# Revit family: ACV-5-Series
name_source: partatom
category: Generic Models
revit_build: Autodesk Revit 2014 (Build: 20130308_1515(x64)
units: mm (PartAtom-declared; Revit-internal decimal feet)

## types (5) — shared parameters
Description = BEECO ACV Angle Series
Manufacturer = MIFAB
Mateiral = Iron, Cast
URL = www.mifab.com

## per-type parameters (varying)
- ACV2.00-HF5PR: 11L=2.15 "; 1L=0.87 "; 2L=1 "; 2RA=3 "; 3L=0.16 "; 3LL=2.09 "; 3LR=3 "; 4H=1 "; 4LONG=2.75 "; 4LONGG=2.25 "; 4THK=0.5 "; 5R=2.85 "; 5RP=0.4 "; 5THK=0.35 "; 6H=0.35 "; 6THK=0.45 "; 7EXT=1.25 "; 7ID=0.45 "; 7OD=0.3 "; 7RP=1.6 "; 8RP=1.2 "; DIA.=2 "; H=9 "; HOLE=0.12 "; HOLE RAD=2.5 "; L=7.8 "; R=3.3 "; R1=2 "; RA=3 "; RADIUS=1 "; RIB THK=0.45 "; W=6.5 "; ext end=10.45 "; ext start=9.38 "
- ACV2.50-HF5PR: 11L=2.15 "; 1L=0.55 "; 2L=1.25 "; 2RA=2.75 "; 3L=0.75 "; 3LL=1.65 "; 3LR=3 "; 4H=1.25 "; 4LONG=2.75 "; 4LONGG=2.25 "; 4THK=0.5 "; 5R=2.85 "; 5RP=0.5 "; 5THK=0.45 "; 6H=0.4 "; 6THK=0.45 "; 7EXT=1.4 "; 7ID=0.5 "; 7OD=0.35 "; 7RP=1.7 "; 8RP=1.3 "; DIA.=2.5 "; H=10 "; HOLE=0.15 "; HOLE RAD=2.5 "; L=8.2 "; R=3.6 "; R1=2.25 "; RA=4 "; RADIUS=1.25 "; RIB THK=0.55 "; W=7.75 "; ext end=10.75 "; ext start=9.5 "
- ACV3.00-HF5PR: 11L=1.6 "; 1L=0.85 "; 2L=1.6 "; 2RA=3 "; 3L=0.75 "; 3LL=2 "; 3LR=4 "; 4H=1.15 "; 4LONG=3.16 "; 4LONGG=2.25 "; 4THK=0.65 "; 5R=3.5 "; 5RP=0.5 "; 5THK=0.45 "; 6H=0.5 "; 6THK=0.65 "; 7EXT=1.52 "; 7ID=0.55 "; 7OD=0.4 "; 7RP=2.25 "; 8RP=1.6 "; DIA.=3 "; H=11.4 "; HOLE=0.25 "; HOLE RAD=3 "; L=11.2 "; R=4.1 "; R1=2.5 "; RA=5 "; RADIUS=1.5 "; RIB THK=0.65 "; W=7.8 "; ext end=10.5 "; ext start=11.75 "
- ACV4.00-HF5PR: 11L=2.55 "; 1L=0.75 "; 2L=1.6 "; 2RA=3 "; 3L=0.5 "; 3LL=2.15 "; 3LR=7 "; 4H=1.65 "; 4LONG=3.16 "; 4LONGG=2 "; 4THK=0.65 "; 5R=4 "; 5RP=0.6 "; 5THK=0.55 "; 6H=0.5 "; 6THK=0.65 "; 7EXT=1.52 "; 7ID=0.65 "; 7OD=0.5 "; 7RP=2.5 "; 8RP=2 "; DIA.=4 "; H=13 "; HOLE=0.3 "; HOLE RAD=3.5 "; L=11.8 "; R=4.3 "; R1=3 "; RA=6 "; RADIUS=2 "; RIB THK=0.75 "; W=8.6 "; ext end=11 "; ext start=12.25 "
- ACV6.00-HF5PR: 11L=3.15 "; 1L=0.85 "; 2L=2 "; 2RA=3 "; 3L=0.75 "; 3LL=3 "; 3LR=10 "; 4H=2.35 "; 4LONG=3.16 "; 4LONGG=2.25 "; 4THK=0.65 "; 5R=4.75 "; 5RP=0.8 "; 5THK=0.75 "; 6H=1 "; 6THK=1 "; 7EXT=1.6 "; 7ID=0.85 "; 7OD=0.65 "; 7RP=3 "; 8RP=3 "; DIA.=6 "; H=17.1 "; HOLE=0.28 "; HOLE RAD=4.25 "; L=15.1 "; R=5.7 "; R1=4 "; RA=8 "; RADIUS=3 "; RIB THK=1 "; W=11.1 "; ext end=12.5 "; ext start=14.25 "

note: column(s) folded — value = type name in every type: Model

## geometry (parser evidence)
native form markers: Sweep x1
no freeform markers — native parametric forms only
